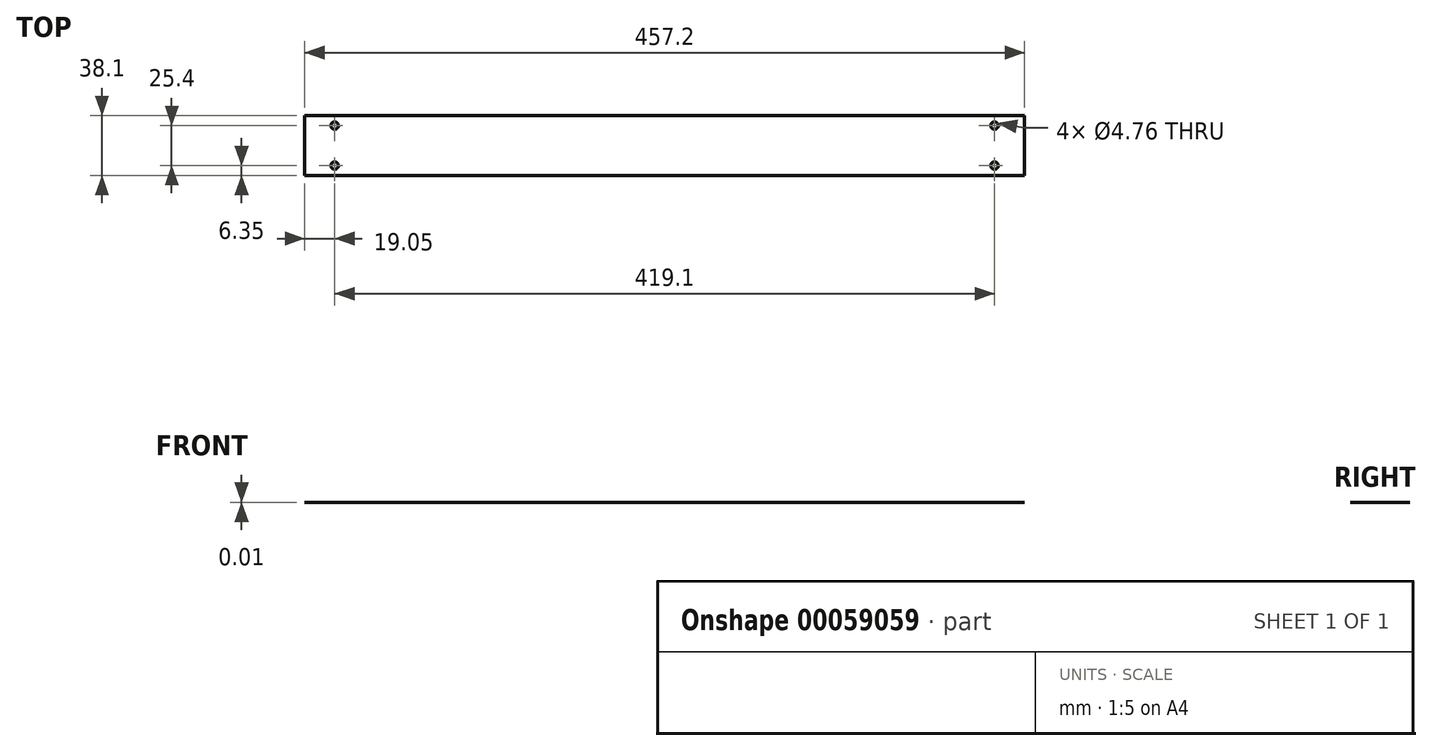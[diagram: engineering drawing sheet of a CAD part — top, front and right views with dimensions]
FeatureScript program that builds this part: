
annotation { "Feature Type Name" : "Feature", "Feature Type Description" : "" }
export const myFeature = defineFeature(function(context is Context, id is Id, definition is map)
    precondition{}
    {
        {
            var Q0;
            Q0=qCreatedBy(makeId("Top.planeOp"),FACE);
            var sketch = newSketch(context, id + "F0", { "sketchPlane" : qUnion([Q0])});
            skLineSegment(sketch, "E0.bottom", {"start": v(228.6, -19.05) * mm, "end": v(-228.6, -19.05) * mm});
            skLineSegment(sketch, "E0.top", {"start": v(228.6, 19.05) * mm, "end": v(-228.6, 19.05) * mm});
            skLineSegment(sketch, "E0.left", {"start": v(228.6, -19.05) * mm, "end": v(228.6, 19.05) * mm});
            skLineSegment(sketch, "E0.right", {"start": v(-228.6, -19.05) * mm, "end": v(-228.6, 19.05) * mm});
            skPoint(sketch, "E0.middle", {"position": v(0, 0) * mm});
            skCircle(sketch, "E1", {"center": v(209.55, 12.7) * mm, "radius": 2.38 * mm});
            skCircle(sketch, "E2.MirrorC", {"center": v(209.55, -12.7) * mm, "radius": 2.38 * mm});
            skCircle(sketch, "E3.MirrorC", {"center": v(-209.55, 12.7) * mm, "radius": 2.38 * mm});
            skCircle(sketch, "E4.MirrorC", {"center": v(-209.55, -12.7) * mm, "radius": 2.38 * mm});
            skSolve(sketch);
        }
        {
            var Q0;
            Q0=makeQuery(id+"F0.imprint","IMPRINT",FACE,{"disambiguationData":[TD([[makeQuery(id+"F0.imprint","IMPRINT",EDGE,{"derivedFrom":sQuery(id+"F0.wireOp",EDGE,"E0.bottom")}),-1.0]])]});
            extrude(context, id + "F1", {"entities" : qUnion([Q0]), "depth" : 3 / 406.4 * mm, "offsetDistance" : 25.4 * mm});
        }
    });
